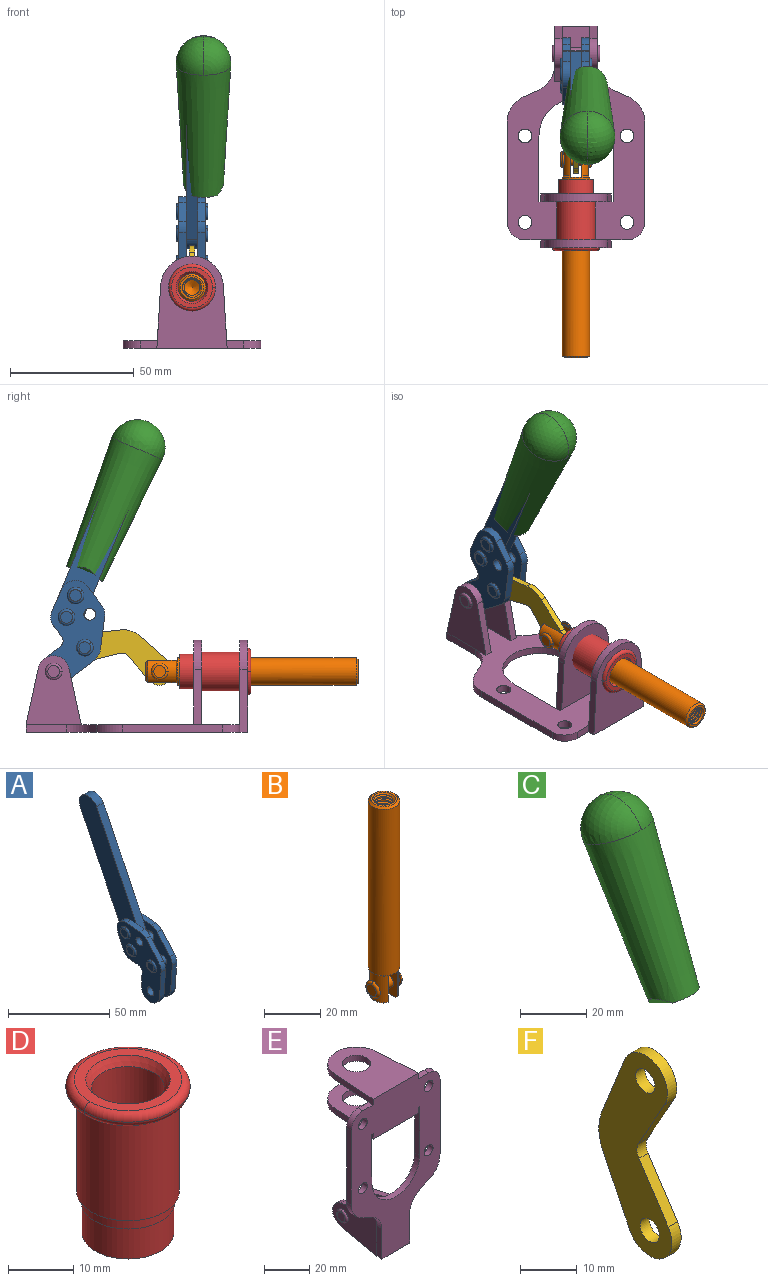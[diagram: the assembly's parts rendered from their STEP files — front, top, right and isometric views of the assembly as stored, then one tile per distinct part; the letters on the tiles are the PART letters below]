
ASSEMBLY  parts=6 mates=6
PART A: 59 faces, bbox 12.9x60.2x99.6 mm
  f0: torus R=2.39mm, axis (-1,0,0), area 14.9mm2, adj f20,f43,f51
  f1: torus R=2.39mm, axis (-1,0,0), area 14.9mm2, adj f19,f42,f51
  f2: torus R=2.39mm, axis (-1,0,0), area 14.9mm2, adj f18,f35,f51
  f3: torus R=2.39mm, axis (-1,0,0), area 14.9mm2, adj f14,f17,f23
  f4: torus R=2.39mm, axis (-1,0,0), area 14.9mm2, adj f13,f16,f23
  f5: torus R=2.39mm, axis (-1,0,0), area 14.9mm2, adj f12,f15,f23
  f6: cylinder r=2.39mm len=4.78mm, axis (1,0,0), area 46.5mm2, adj f48,f50,f51
  f7: cylinder r=2.39mm len=4.78mm, axis (1,0,0), area 46.5mm2, adj f50,f51
  f8: cylinder r=6.35mm len=12.68mm, axis (1,0,0), area 61.8mm2, adj f38,f39,f50,f51
  f9: cylinder r=2.39mm len=4.78mm, axis (-1,0,0), area 70.5mm2, adj f46,f50
  f10: cylinder r=2.39mm len=4.78mm, axis (-1,0,0), area 46.5mm2, adj f23,f45,f46
  f11: cylinder r=2.39mm len=4.78mm, axis (-1,0,0), area 46.5mm2, adj f23,f46
  f12: plane 4.78x4.78mm, normal (1,0,0), area 17.9mm2, adj f5,f15
  f13: plane 4.78x4.78mm, normal (1,0,0), area 17.9mm2, adj f4,f16
  f14: plane 4.78x4.78mm, normal (1,0,0), area 17.9mm2, adj f3,f17
  f15: torus R=2.39mm, axis (-1,0,0), area 14.9mm2, adj f5,f12,f23
  f16: torus R=2.39mm, axis (-1,0,0), area 14.9mm2, adj f4,f13,f23
  f17: torus R=2.39mm, axis (-1,0,0), area 14.9mm2, adj f3,f14,f23
  f18: plane 4.78x4.78mm, normal (-1,0,0), area 17.9mm2, adj f2,f35
  f19: plane 4.78x4.78mm, normal (-1,0,0), area 17.9mm2, adj f1,f42
  f20: plane 4.78x4.78mm, normal (-1,0,0), area 17.9mm2, adj f0,f43
  f21: plane 2.26x0.2mm, normal (1,0,0), area 0.2mm2, adj f31,f44
  f22: plane 2.26x0.2mm, normal (-1,0,0), area 0.2mm2, adj f41,f44
  f23: plane 39.37x30.77mm, normal (1,0,0), area 565.5mm2, adj f3,f4,f5,f10,f11,f15,f16,f17
  f24: cylinder r=6.1mm len=4.15mm, axis (-1,0,0), area 14.7mm2, adj f23,f25,f32,f46
  f25: plane 10.25x9.01mm, normal (0,-0.75,0.66), area 42.3mm2, adj f23,f24,f26,f46
  f26: cylinder r=6.35mm len=4.64mm, axis (-1,0,0), area 15.6mm2, adj f23,f25,f27,f46
  f27: plane 15.84x3.1mm, normal (0,-1,-0.07), area 49.2mm2, adj f23,f26,f28,f46
  f28: cylinder r=6.35mm len=12.68mm, axis (-1,0,0), area 61.8mm2, adj f23,f27,f29,f46
  f29: plane 8.11x3.1mm, normal (0,1,0.07), area 25.2mm2, adj f23,f28,f30,f46
  f30: cylinder r=3.05mm len=3.25mm, axis (-1,0,0), area 14.8mm2, adj f23,f29,f31,f46
  f31: plane 5.99x3.1mm, normal (0,0.07,-1), area 18.6mm2, adj f21,f23,f30,f44,f46
  f32: plane 9.5x3.1mm, normal (0,-0.07,1), area 29.5mm2, adj f23,f24,f33,f46,f47
  f33: cylinder r=6.1mm len=8.63mm, axis (-1,0,0), area 39.1mm2, adj f23,f32,f34,f47
  f34: plane 8.65x3.96mm, normal (0,0.91,-0.42), area 29.5mm2, adj f23,f33,f44,f47
  f35: torus R=2.39mm, axis (-1,0,0), area 14.9mm2, adj f2,f18,f51
  f36: plane 10.25x9.01mm, normal (0,-0.75,0.66), area 42.3mm2, adj f37,f49,f50,f51
  f37: cylinder r=6.35mm len=4.64mm, axis (1,0,0), area 15.6mm2, adj f36,f38,f50,f51
  f38: plane 15.84x3.1mm, normal (0,-1,-0.07), area 49.2mm2, adj f8,f37,f50,f51
  f39: plane 8.11x3.1mm, normal (0,1,0.07), area 25.2mm2, adj f8,f40,f50,f51
  f40: cylinder r=3.05mm len=3.25mm, axis (1,0,0), area 14.8mm2, adj f39,f41,f50,f51
  f41: plane 5.99x3.1mm, normal (0,0.07,-1), area 18.6mm2, adj f22,f40,f44,f50,f51
  f42: torus R=2.39mm, axis (-1,0,0), area 14.9mm2, adj f1,f19,f51
  f43: torus R=2.39mm, axis (-1,0,0), area 14.9mm2, adj f0,f20,f51
  f44: cylinder r=6.35mm len=12.12mm, axis (-1,0,0), area 128.9mm2, adj f21,f22,f23,f31,f34,f41,f46,f47
  f45: plane 2.65x1.35mm, normal (1,0,0), area 1mm2, adj f10,f55
  f46: plane 39.08x20.42mm, normal (-1,0,0), area 412.5mm2, adj f9,f10,f11,f24,f25,f26,f27,f28
  f47: plane 77.62x39.82mm, normal (1,0,0), area 850mm2, adj f32,f33,f34,f44,f53,f54,f55
  f48: plane 2.65x1.35mm, normal (-1,0,0), area 1mm2, adj f6,f55
  f49: cylinder r=6.1mm len=4.15mm, axis (1,0,0), area 14.7mm2, adj f36,f50,f51,f56
  f50: plane 39.08x20.42mm, normal (1,0,0), area 412.5mm2, adj f6,f7,f8,f9,f36,f37,f38,f39
  f51: plane 39.37x30.77mm, normal (-1,0,0), area 565.5mm2, adj f0,f1,f2,f6,f7,f8,f35,f36
  f52: plane 8.65x3.96mm, normal (0,0.91,-0.42), area 29.5mm2, adj f44,f51,f57,f58
  f53: plane 68.49x33.4mm, normal (0,0.9,-0.44), area 358.1mm2, adj f44,f47,f54,f58
  f54: cylinder r=6.35mm len=12.06mm, axis (1,0,0), area 93.7mm2, adj f47,f53,f55,f58
  f55: plane 68.49x33.4mm, normal (0,-0.9,0.44), area 358.1mm2, adj f44,f45,f46,f47,f48,f50,f54,f58
  f56: plane 9.5x3.1mm, normal (0,-0.07,1), area 29.5mm2, adj f49,f50,f51,f57,f58
  f57: cylinder r=6.1mm len=8.63mm, axis (1,0,0), area 39.1mm2, adj f51,f52,f56,f58
  f58: plane 77.62x39.82mm, normal (-1,0,0), area 850mm2, adj f44,f52,f53,f54,f55,f56,f57
PART B: 48 faces, bbox 12.6x11.1x86.1 mm
  f0: torus R=2.41mm, axis (-1,0,0), area 15mm2, adj f30,f32,f34
  f1: torus R=2.41mm, axis (-1,0,0), area 15mm2, adj f29,f31,f33
  f2: cylinder r=5.54mm len=72.39mm, axis (0,0,1), area 2518.5mm2, adj f3,f4,f42,f43
  f3: cone r=5.54mm half-angle=45deg, axis (0,0,1), area 7.6mm2, adj f2,f5,f41
  f4: cone r=5.54mm half-angle=45deg, axis (0,0,-1), area 34.9mm2, adj f2,f39
  f5: cylinder r=5.08mm len=11.48mm, axis (0,0,1), area 108.3mm2, adj f3,f7,f8,f41
  f6: cylinder r=2.41mm len=4.83mm, axis (-1,0,0), area 71.2mm2, adj f40,f41
  f7: cylinder r=2.41mm len=4.83mm, axis (-1,0,0), area 7.6mm2, adj f5,f34
  f8: cone r=5.08mm half-angle=45deg, axis (0,0,1), area 10.6mm2, adj f5,f37,f41
  f9: cone r=3.98mm half-angle=45deg, axis (0,0,1), area 17.6mm2, adj f27,f39,f45,f46,f47
  f10: cylinder r=2.41mm len=4.83mm, axis (-1,0,0), area 7.6mm2, adj f33,f38
  f11: cylinder r=3.2mm len=6.4mm, axis (0,0,1), area 78.4mm2, adj f12,f28,f44,f45,f47
  f12: cylinder r=3.2mm len=6.4mm, axis (0,0,1), area 10.5mm2, adj f11,f13,f45,f47
  f13: cylinder r=3.2mm len=6.4mm, axis (0,0,1), area 10.5mm2, adj f12,f14,f45,f47
  f14: cylinder r=3.2mm len=6.4mm, axis (0,0,1), area 10.5mm2, adj f13,f15,f45,f47
  f15: cylinder r=3.2mm len=6.4mm, axis (0,0,1), area 10.5mm2, adj f14,f16,f45,f47
  f16: cylinder r=3.2mm len=6.4mm, axis (0,0,1), area 10.5mm2, adj f15,f17,f45,f47
  f17: cylinder r=3.2mm len=6.4mm, axis (0,0,1), area 10.5mm2, adj f16,f18,f45,f47
  f18: cylinder r=3.2mm len=6.4mm, axis (0,0,1), area 10.5mm2, adj f17,f19,f45,f47
  f19: cylinder r=3.2mm len=6.4mm, axis (0,0,1), area 10.5mm2, adj f18,f20,f45,f47
  f20: cylinder r=3.2mm len=6.4mm, axis (0,0,1), area 10.5mm2, adj f19,f21,f45,f47
  f21: cylinder r=3.2mm len=6.4mm, axis (0,0,1), area 10.5mm2, adj f20,f22,f45,f47
  f22: cylinder r=3.2mm len=6.4mm, axis (0,0,1), area 10.5mm2, adj f21,f23,f45,f47
  f23: cylinder r=3.2mm len=6.4mm, axis (0,0,1), area 10.5mm2, adj f22,f24,f45,f47
  f24: cylinder r=3.2mm len=6.4mm, axis (0,0,1), area 10.5mm2, adj f23,f25,f45,f47
  f25: cylinder r=3.2mm len=6.4mm, axis (0,0,1), area 10.5mm2, adj f24,f26,f45,f47
  f26: cylinder r=3.2mm len=6.4mm, axis (0,0,1), area 10.5mm2, adj f25,f27,f45,f47
  f27: cylinder r=3.2mm len=6.4mm, axis (0,0,1), area 7.4mm2, adj f9,f26,f45,f47
  f28: cone r=3.2mm half-angle=60deg, axis (0,0,1), area 37.2mm2, adj f11
  f29: plane 4.83x4.83mm, normal (-1,0,0), area 18.3mm2, adj f1,f31
  f30: plane 4.83x4.83mm, normal (1,0,0), area 18.3mm2, adj f0,f32
  f31: torus R=2.41mm, axis (-1,0,0), area 15mm2, adj f1,f29,f33
  f32: torus R=2.41mm, axis (-1,0,0), area 15mm2, adj f0,f30,f34
  f33: plane 6.83x6.83mm, normal (1,0,0), area 18.3mm2, adj f1,f10,f31
  f34: plane 6.83x6.83mm, normal (-1,0,0), area 18.3mm2, adj f0,f7,f32
  f35: cone r=5.08mm half-angle=45deg, axis (0,0,1), area 10.6mm2, adj f36,f38,f40
  f36: plane 7.25x1.97mm, normal (0,0,-1), area 10mm2, adj f35,f40
  f37: plane 7.25x1.97mm, normal (0,0,-1), area 10mm2, adj f8,f41
  f38: cylinder r=5.08mm len=11.48mm, axis (0,0,1), area 108.3mm2, adj f10,f35,f40,f42
  f39: plane 9.55x9.55mm, normal (0,0,1), area 22mm2, adj f4,f9
  f40: plane 12.76x10.09mm, normal (1,0,0), area 95.7mm2, adj f6,f35,f36,f38,f42,f43
  f41: plane 12.76x10.09mm, normal (-1,0,0), area 95.7mm2, adj f3,f5,f6,f8,f37,f43
  f42: cone r=5.54mm half-angle=45deg, axis (0,0,1), area 7.6mm2, adj f2,f38,f40
  f43: plane 11.07x4.7mm, normal (0,0,-1), area 50.4mm2, adj f2,f40,f41
  f44: plane 0.89x0.62mm, normal (-1,0,0), area 0.3mm2, adj f11,f45,f46,f47
  f45: bspline ~24.8x7.63mm, area 266.6mm2, adj f9,f11,f12,f13,f14,f15,f16,f17
  f46: bspline ~24.87x7.63mm, area 73.6mm2, adj f9,f44,f45,f47
  f47: bspline ~24.98x7.63mm, area 272.5mm2, adj f9,f11,f12,f13,f14,f15,f16,f17
PART C: 11 faces, bbox 22.3x42.6x64.5 mm
  f0: sphere r=11.13mm, area 411.4mm2, adj f1,f8
  f1: cone r=11.11mm half-angle=3.3deg, axis (0,0.44,0.9), area 3251.8mm2, adj f0,f7,f8,f9,f10
  f2: cylinder r=6.16mm len=11.7mm, axis (1,0,0), area 89.5mm2, adj f3,f4,f5,f6
  f3: plane 60.23x36.75mm, normal (-1,0,0), area 763.6mm2, adj f2,f4,f6,f10
  f4: plane 51.37x25.05mm, normal (0,0.9,-0.44), area 264.2mm2, adj f2,f3,f5,f10
  f5: plane 60.23x36.75mm, normal (1,0,0), area 763.6mm2, adj f2,f4,f6,f10
  f6: plane 51.37x25.05mm, normal (0,-0.9,0.44), area 264.2mm2, adj f2,f3,f5,f10
  f7: plane 9.95x5.95mm, normal (0.71,-0.31,-0.64), area 25.8mm2, adj f1,f10
  f8: sphere r=11.13mm, area 411.4mm2, adj f0,f1
  f9: plane 9.95x5.95mm, normal (-0.71,-0.31,-0.64), area 25.8mm2, adj f1,f10
  f10: plane 14.27x11.38mm, normal (0,-0.44,-0.9), area 106.7mm2, adj f1,f3,f4,f5,f6,f7,f9
PART D: 15 faces, bbox 20.6x20.6x28.7 mm
  f0: torus R=8.26mm, axis (0,0,1), area 56.8mm2, adj f1,f10,f12
  f1: torus R=8.26mm, axis (0,0,1), area 56.8mm2, adj f0,f6,f13
  f2: cylinder r=5.59mm len=25.91mm, axis (0,0,1), area 909.6mm2, adj f3,f4
  f3: cone r=6.86mm half-angle=45deg, axis (0,0,-1), area 70.2mm2, adj f2,f14
  f4: cone r=6.47mm half-angle=30deg, axis (0,0,1), area 66.7mm2, adj f2,f13
  f5: cylinder r=7.04mm len=14.07mm, axis (0,0,1), area 252.6mm2, adj f11,f14
  f6: torus R=8.26mm, axis (0,0,1), area 56.8mm2, adj f1,f12,f13
  f7: cylinder r=7.16mm len=14.33mm, axis (0,0,1), area 91.5mm2, adj f9,f11
  f8: cylinder r=7.86mm len=18.42mm, axis (0,0,1), area 909.6mm2, adj f9,f10
  f9: plane 15.72x15.72mm, normal (0,0,-1), area 33mm2, adj f7,f8
  f10: plane 16.51x16.51mm, normal (0,0,-1), area 19.9mm2, adj f0,f8,f12
  f11: plane 14.33x14.33mm, normal (0,0,-1), area 5.7mm2, adj f5,f7
  f12: torus R=8.26mm, axis (0,0,1), area 56.8mm2, adj f0,f6,f10
  f13: plane 16.51x16.51mm, normal (0,0,1), area 82.7mm2, adj f1,f4,f6
  f14: plane 14.07x14.07mm, normal (0,0,-1), area 7.8mm2, adj f3,f5
PART E: 55 faces, bbox 55.7x37.4x89.8 mm
  f0: torus R=2.41mm, axis (-1,0,0), area 15mm2, adj f11,f15,f25
  f1: torus R=2.41mm, axis (-1,0,0), area 15mm2, adj f10,f12,f22
  f2: cylinder r=2.78mm len=5.56mm, axis (0,-1,0), area 54.2mm2, adj f30,f54
  f3: cylinder r=14.99mm len=29.97mm, axis (0,-1,0), area 145.9mm2, adj f30,f49,f53,f54
  f4: cylinder r=2.78mm len=5.56mm, axis (0,-1,0), area 54.2mm2, adj f30,f54
  f5: cylinder r=2.78mm len=5.56mm, axis (0,-1,0), area 54.2mm2, adj f30,f54
  f6: cylinder r=2.78mm len=5.56mm, axis (0,-1,0), area 54.2mm2, adj f30,f54
  f7: cylinder r=6.35mm len=12.7mm, axis (0,0,1), area 123.6mm2, adj f27,f51
  f8: cylinder r=6.35mm len=12.7mm, axis (0,0,-1), area 124.7mm2, adj f21,f35
  f9: cylinder r=2.41mm len=11.18mm, axis (-1,0,0), area 169.4mm2, adj f16,f19
  f10: plane 4.83x4.83mm, normal (1,0,0), area 18.3mm2, adj f1,f12
  f11: plane 4.83x4.83mm, normal (-1,0,0), area 18.3mm2, adj f0,f15
  f12: torus R=2.41mm, axis (-1,0,0), area 15mm2, adj f1,f10,f22
  f13: cylinder r=6.35mm len=12.41mm, axis (1,0,0), area 53.4mm2, adj f18,f19,f22,f23
  f14: cylinder r=6.35mm len=12.41mm, axis (-1,0,0), area 53.4mm2, adj f16,f17,f24,f25
  f15: torus R=2.41mm, axis (-1,0,0), area 15mm2, adj f0,f11,f25
  f16: plane 27.86x22.35mm, normal (1,0,0), area 425.4mm2, adj f9,f14,f17,f24,f30
  f17: plane 22.86x4.97mm, normal (0,0.21,0.98), area 72.5mm2, adj f14,f16,f25,f30
  f18: plane 22.86x4.97mm, normal (0,0.21,0.98), area 72.5mm2, adj f13,f19,f22,f30
  f19: plane 27.86x22.35mm, normal (-1,0,0), area 425.4mm2, adj f9,f13,f18,f23,f30
  f20: cylinder r=12.7mm len=25.35mm, axis (0,0,-1), area 119.8mm2, adj f21,f34,f35,f36
  f21: plane 34.21x28.07mm, normal (0,0,-1), area 702.4mm2, adj f8,f20,f30,f34,f36
  f22: plane 27.96x22.45mm, normal (1,0,0), area 407.2mm2, adj f1,f12,f13,f18,f23,f30,f42,f43
  f23: plane 22.86x4.97mm, normal (0,0.21,-0.98), area 72.5mm2, adj f13,f19,f22,f44
  f24: plane 22.86x4.97mm, normal (0,0.21,-0.98), area 72.5mm2, adj f14,f16,f25,f44
  f25: plane 27.86x22.35mm, normal (-1,0,0), area 407.1mm2, adj f0,f14,f15,f17,f24,f30,f45,f46
  f26: plane 3.1x0.95mm, normal (0,0,-1), area 2.7mm2, adj f30,f49,f50,f54
  f27: plane 34.21x28.07mm, normal (0,0,1), area 702.4mm2, adj f7,f28,f30,f50,f52
  f28: cylinder r=12.7mm len=25.35mm, axis (0,0,1), area 118.8mm2, adj f27,f50,f51,f52
  f29: plane 3.1x0.95mm, normal (0,0,-1), area 2.7mm2, adj f30,f52,f53,f54
  f30: plane 86.54x55.63mm, normal (0,1,0), area 2362.9mm2, adj f2,f3,f4,f5,f6,f16,f17,f18
  f31: plane 40.56x3.1mm, normal (-1,0,0), area 125.7mm2, adj f30,f32,f48,f54
  f32: cylinder r=7.11mm len=7.11mm, axis (0,-1,0), area 34.6mm2, adj f30,f31,f33,f54
  f33: plane 6.67x3.1mm, normal (0,0,1), area 20.4mm2, adj f30,f32,f34,f54
  f34: plane 25.39x3.13mm, normal (-1,0.06,0), area 79.5mm2, adj f20,f21,f33,f35,f54
  f35: plane 37.31x28.45mm, normal (0,0,1), area 789.9mm2, adj f8,f20,f34,f36,f54
  f36: plane 25.39x3.13mm, normal (1,0.06,0), area 79.5mm2, adj f20,f21,f35,f37,f54
  f37: plane 6.67x3.1mm, normal (0,0,1), area 20.4mm2, adj f30,f36,f38,f54
  f38: cylinder r=7.11mm len=7.11mm, axis (0,-1,0), area 34.6mm2, adj f30,f37,f39,f54
  f39: plane 40.56x3.1mm, normal (1,0,0), area 125.7mm2, adj f30,f38,f40,f54
  f40: cylinder r=11.18mm len=10.16mm, axis (0,-1,0), area 39.5mm2, adj f30,f39,f41,f54
  f41: plane 6.09x3.1mm, normal (0.42,0,-0.91), area 20.8mm2, adj f30,f40,f42,f54
  f42: cylinder r=11.18mm len=9.41mm, axis (0,-1,0), area 37.2mm2, adj f22,f30,f41,f43,f54
  f43: plane 16.5x3.1mm, normal (1,0,0), area 51.1mm2, adj f22,f42,f44,f54
  f44: plane 17.37x3.1mm, normal (0,0,-1), area 53.8mm2, adj f23,f24,f30,f43,f45,f54
  f45: plane 16.5x3.1mm, normal (-1,0,0), area 51.1mm2, adj f25,f44,f46,f54
  f46: cylinder r=11.18mm len=9.41mm, axis (0,-1,0), area 37.2mm2, adj f25,f30,f45,f47,f54
  f47: plane 6.09x3.1mm, normal (-0.42,0,-0.91), area 20.8mm2, adj f30,f46,f48,f54
  f48: cylinder r=11.18mm len=10.16mm, axis (0,-1,0), area 39.5mm2, adj f30,f31,f47,f54
  f49: plane 26.54x3.1mm, normal (-1,0,0), area 82.3mm2, adj f3,f26,f30,f54
  f50: plane 25.39x3.1mm, normal (1,0.06,0), area 78.8mm2, adj f26,f27,f28,f51,f54
  f51: plane 37.31x28.45mm, normal (0,0,-1), area 789.9mm2, adj f7,f28,f50,f52,f54
  f52: plane 25.39x3.1mm, normal (-1,0.06,0), area 78.8mm2, adj f27,f28,f29,f51,f54
  f53: plane 26.54x3.1mm, normal (1,0,0), area 82.3mm2, adj f3,f29,f30,f54
  f54: plane 89.66x55.63mm, normal (0,-1,0), area 2678.5mm2, adj f2,f3,f4,f5,f6,f26,f29,f31
PART F: 12 faces, bbox 2.3x18.2x42.8 mm
  f0: cylinder r=2.4mm len=4.8mm, axis (1,0,0), area 34.9mm2, adj f4,f11
  f1: cylinder r=10.41mm len=8.47mm, axis (1,0,0), area 20.2mm2, adj f4,f9,f10,f11
  f2: cylinder r=3.05mm len=3.16mm, axis (1,0,0), area 7.7mm2, adj f4,f6,f7,f11
  f3: cylinder r=2.4mm len=4.8mm, axis (1,0,0), area 34.9mm2, adj f4,f11
  f4: plane 42.81x18.23mm, normal (-1,0,0), area 414.1mm2, adj f0,f1,f2,f3,f5,f6,f7,f8
  f5: cylinder r=5.54mm len=10.67mm, axis (1,0,0), area 41.8mm2, adj f4,f6,f10,f11
  f6: plane 11.66x6.53mm, normal (0,-0.87,-0.49), area 30.9mm2, adj f2,f4,f5,f11
  f7: plane 11.17x7.33mm, normal (0,-0.84,0.55), area 30.9mm2, adj f2,f4,f8,f11
  f8: cylinder r=5.54mm len=10.51mm, axis (1,0,0), area 41.8mm2, adj f4,f7,f9,f11
  f9: plane 13.67x6.67mm, normal (0,0.9,-0.44), area 35.1mm2, adj f1,f4,f8,f11
  f10: plane 14.1x5.7mm, normal (0,0.93,0.37), area 35.1mm2, adj f1,f4,f5,f11
  f11: plane 42.81x18.23mm, normal (1,0,0), area 414.1mm2, adj f0,f1,f2,f3,f5,f6,f7,f8
PLACE A rot(axis=(1,0,0),48.7deg) t=(0,0.88,27.32)mm
PLACE B rot(axis=(1,0,0),90deg) t=(0,13.83,0)mm
PLACE C rot(axis=(1,0,0),48.7deg) t=(4.66,0.88,27.32)mm
PLACE D rot(axis=(1,0,0),90deg) t=(0,10.41,0)mm
PLACE E rot(axis=(1,0,0),90deg) t=(0,9.14,0)mm fixed
PLACE F rot(axis=(1,0,0),109.6deg) t=(0,21.2,6.64)mm
MATE fastened E.f7 <-> D.f2  axis (0,-1,0) through (0,-37.25,24.61)mm
MATE revolute B.f6 <-> F.f5  axis (-1,0,0) through (0,-1.65,24.61)mm
MATE revolute A.f7 <-> E.f0  axis (1,0,0) through (0,41.23,24.61)mm
MATE fastened A.f54 <-> C.f2  axis (1,0,0) through (2.35,6.65,116.84)mm
MATE revolute A.f4 <-> F.f3  axis (-1,0,0) through (0,28.61,34.24)mm
MATE slider B.f2 <-> E.f7  axis (0,-1,0) through (0,-44.95,24.61)mm
